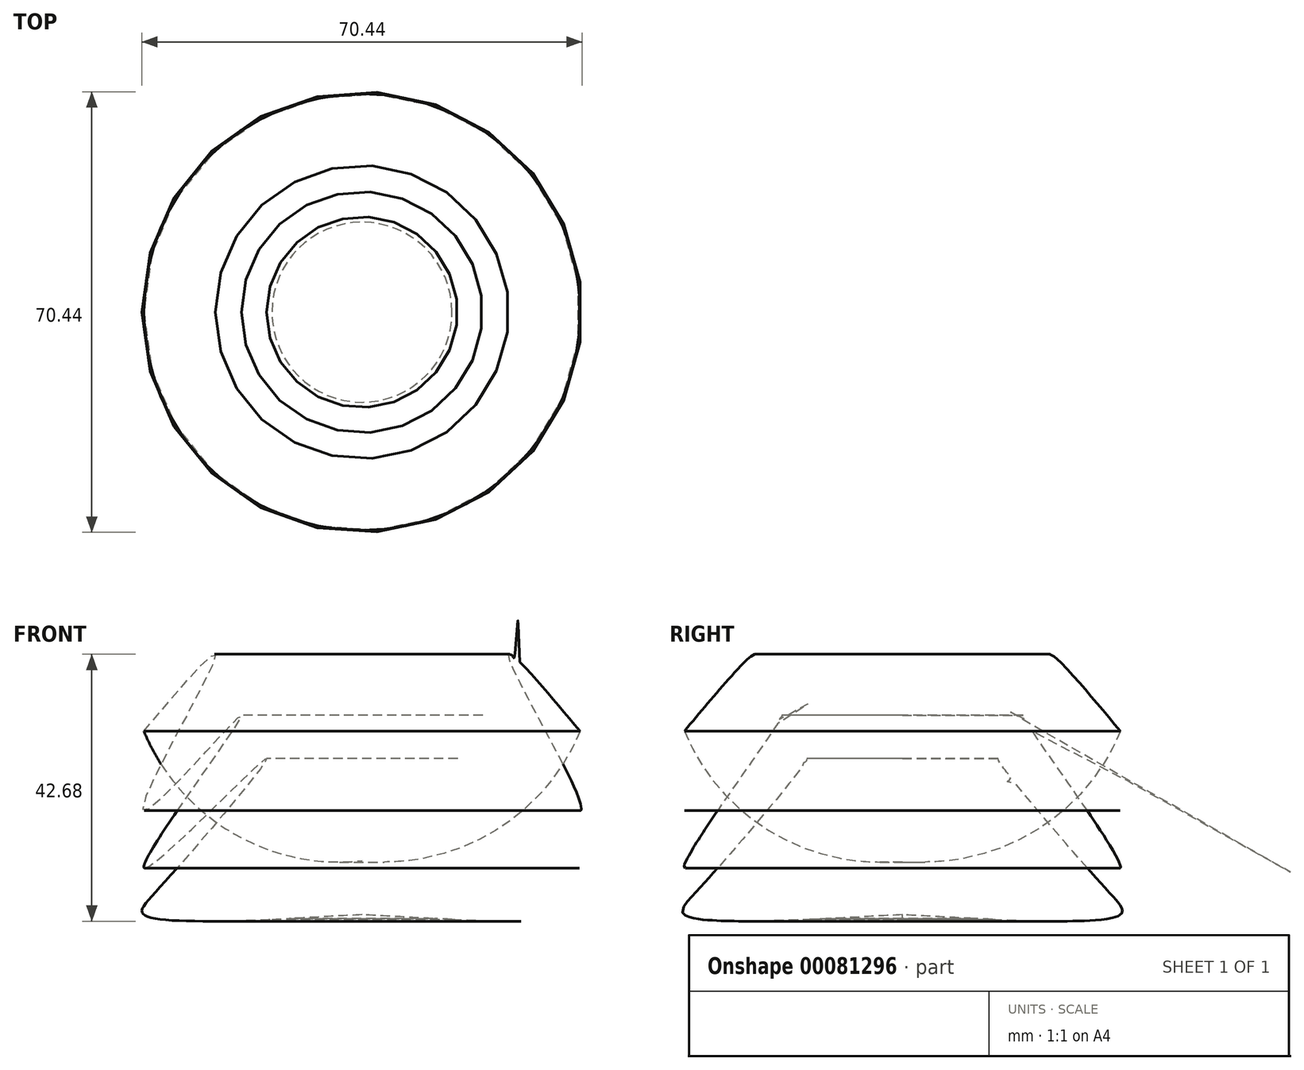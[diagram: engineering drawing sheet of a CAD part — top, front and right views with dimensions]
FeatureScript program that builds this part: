
annotation { "Feature Type Name" : "Feature", "Feature Type Description" : "" }
export const myFeature = defineFeature(function(context is Context, id is Id, definition is map)
    precondition{}
    {
        {
            var Q0;
            Q0=qCreatedBy(makeId("Front.planeOp"),FACE);
            var sketch = newSketch(context, id + "F0", { "sketchPlane" : qUnion([Q0])});
            skLineSegment(sketch, "E0", {"start": v(0, 0) * mm, "end": v(0, 75.94) * mm});
            skArc(sketch, "E1", {"start": v(34.88, 29.35) * mm, "mid": v(30.7, 62.57) * mm, "end": v(0, 75.94) * mm});
            skFitSpline(sketch, "E2", {"points": [v(34.88, 29.35) * mm, v(23.53, 41.01) * mm, v(34.88, 16.64) * mm, v(19.29, 31.9) * mm, v(34.88, 7.52) * mm, v(15.47, 24.9) * mm, v(31.8, 4.98) * mm, v(34.88, 0) * mm, v(0, 0) * mm], "startDerivative": vector(-170.5, 203.93) * mm, "endDerivative": vector(-311, 17.1) * mm});
            skFitSpline(sketch, "E3", {"points": [v(16.2, -0.9) * mm, v(14.4, -0.74) * mm, v(11.67, -0.61) * mm, v(0, 0) * mm], "startDerivative": vector(-8.56, 1.03) * mm, "endDerivative": vector(-25.72, 1.3) * mm});
            skSolve(sketch);
        }
        {
            var Q0;
            {var subQ6=sQuery(id+"F0.wireOp",EDGE,"E0");Q0=makeQuery(id+"F0.imprint","IMPRINT",FACE,{"disambiguationData":[TD([[makeQuery(id+"F0.imprint","IMPRINT",EDGE,{"derivedFrom":subQ6}),-1.0]])]});}
            var Q1;
            Q1=sQuery(id+"F0.wireOp",EDGE,"E0");
            revolve(context, id + "F1", {"entities" : qUnion([Q0]), "axis" : qUnion([Q1]), "revolveType" : RevolveType.FULL});
        }
    });
